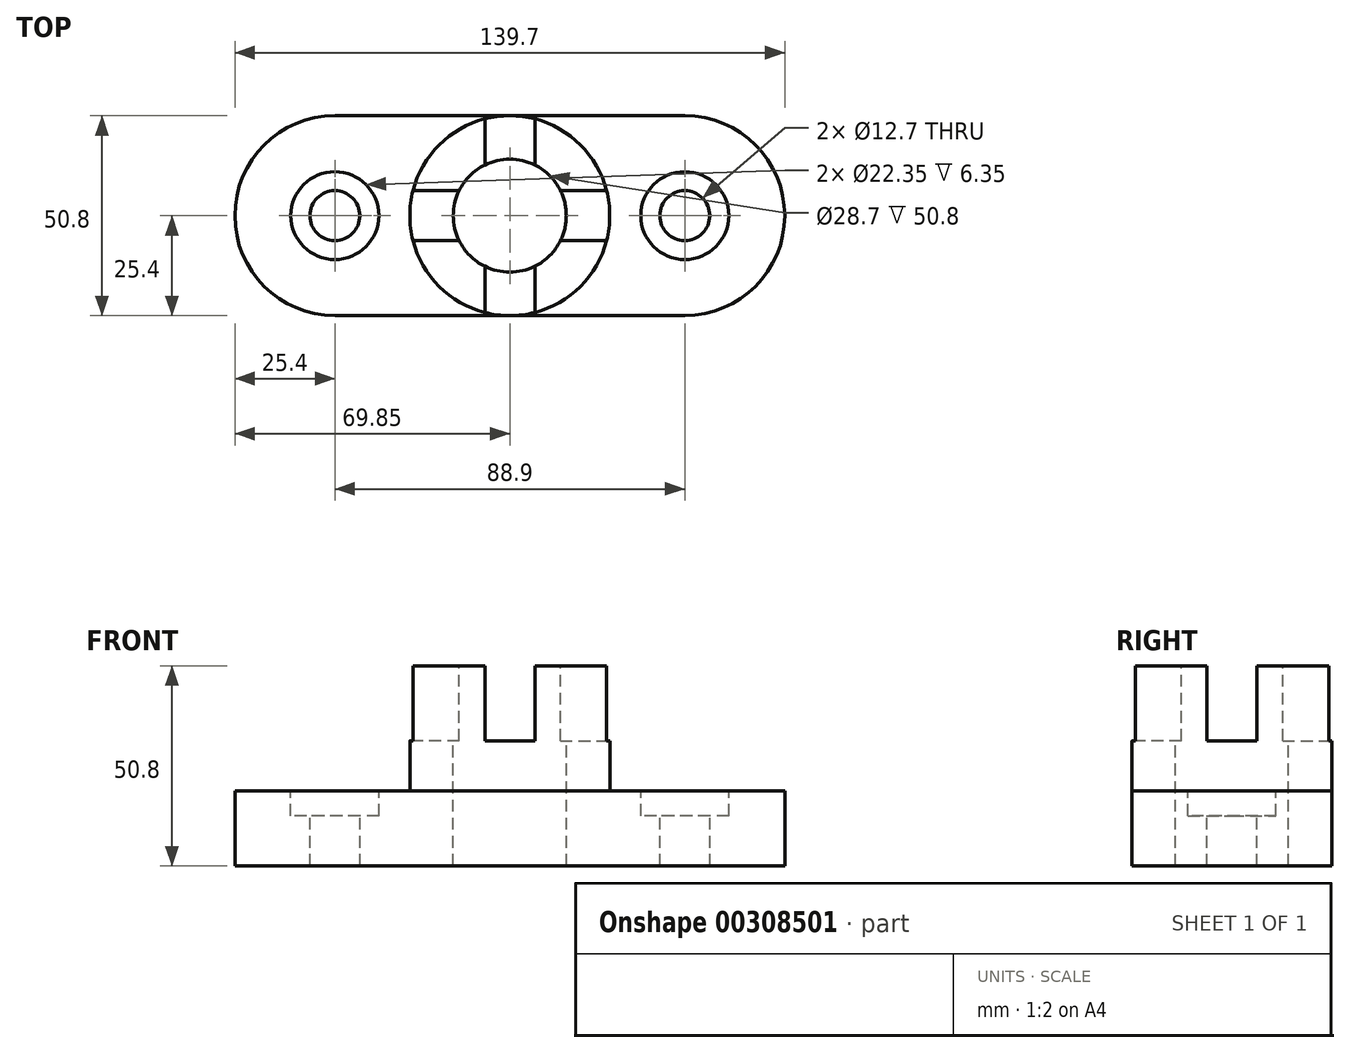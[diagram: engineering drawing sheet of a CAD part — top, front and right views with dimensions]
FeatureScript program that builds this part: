
annotation { "Feature Type Name" : "Feature", "Feature Type Description" : "" }
export const myFeature = defineFeature(function(context is Context, id is Id, definition is map)
    precondition{}
    {
        {
            var Q0;
            Q0=qCreatedBy(makeId("Top.planeOp"),FACE);
            var sketch = newSketch(context, id + "F0", { "sketchPlane" : qUnion([Q0])});
            skLineSegment(sketch, "E0.bottom", {"start": v(-44.45, -25.4) * mm, "end": v(44.45, -25.4) * mm, "construction": true});
            skLineSegment(sketch, "E0.top", {"start": v(-44.45, 25.4) * mm, "end": v(44.45, 25.4) * mm, "construction": true});
            skLineSegment(sketch, "E0.left", {"start": v(-44.45, -25.4) * mm, "end": v(-44.45, 25.4) * mm, "construction": true});
            skLineSegment(sketch, "E0.right", {"start": v(44.45, -25.4) * mm, "end": v(44.45, 25.4) * mm, "construction": true});
            skLineSegment(sketch, "E1.bottom", {"start": v(-69.85, -25.4) * mm, "end": v(69.85, -25.4) * mm, "construction": true});
            skLineSegment(sketch, "E1.top", {"start": v(-69.85, 25.4) * mm, "end": v(69.85, 25.4) * mm, "construction": true});
            skLineSegment(sketch, "E1.left", {"start": v(-69.85, -25.4) * mm, "end": v(-69.85, 25.4) * mm, "construction": true});
            skLineSegment(sketch, "E1.right", {"start": v(69.85, -25.4) * mm, "end": v(69.85, 25.4) * mm, "construction": true});
            skLineSegment(sketch, "E2", {"start": v(-69.85, 0) * mm, "end": v(69.85, 0) * mm, "construction": true});
            skLineSegment(sketch, "E3", {"start": v(-44.45, -25.4) * mm, "end": v(44.45, -25.4) * mm});
            skLineSegment(sketch, "E4", {"start": v(44.45, 25.4) * mm, "end": v(-44.45, 25.4) * mm});
            skArc(sketch, "E5", {"start": v(-44.45, 25.4) * mm, "mid": v(-69.85, 0) * mm, "end": v(-44.45, -25.4) * mm});
            skArc(sketch, "E6", {"start": v(44.45, -25.4) * mm, "mid": v(69.85, 0) * mm, "end": v(44.45, 25.4) * mm});
            skCircle(sketch, "E7", {"center": v(-44.45, 0) * mm, "radius": 11.18 * mm});
            skCircle(sketch, "E8", {"center": v(44.45, 0) * mm, "radius": 11.18 * mm});
            skCircle(sketch, "E9", {"center": v(44.45, 0) * mm, "radius": 6.35 * mm});
            skCircle(sketch, "E10", {"center": v(-44.45, 0) * mm, "radius": 6.35 * mm});
            skCircle(sketch, "E11", {"center": v(0, 0) * mm, "radius": 25.4 * mm});
            skSolve(sketch);
        }
        {
            var Q0;
            Q0=makeQuery(id+"F0.imprint","IMPRINT",FACE,{"disambiguationData":[TD([[makeQuery(id+"F0.imprint","IMPRINT",EDGE,{"derivedFrom":sQuery(id+"F0.wireOp",EDGE,"E3")}),1.0]])]});
            var Q1;
            Q1=makeQuery(id+"F0.imprint","IMPRINT",FACE,{"disambiguationData":[TD([[makeQuery(id+"F0.imprint","IMPRINT",EDGE,{"derivedFrom":sQuery(id+"F0.wireOp",EDGE,"E7")}),1.0]])]});
            var Q2;
            Q2=makeQuery(id+"F0.imprint","IMPRINT",FACE,{"disambiguationData":[TD([[makeQuery(id+"F0.imprint","IMPRINT",EDGE,{"derivedFrom":sQuery(id+"F0.wireOp",EDGE,"E8")}),1.0]])]});
            var Q3;
            {var subQ0=sQuery(id+"F0.wireOp",EDGE,"E11");var subQ1=makeQuery(id+"F0.imprint","INTERSECT",VERTEX,{"derivedFrom":[sQuery(id+"F0.wireOp",EDGE,"E3"),subQ0]});Q3=makeQuery(id+"F0.imprint","IMPRINT",FACE,{"disambiguationData":[TD([[makeQuery(id+"F0.imprint","IMPRINT",EDGE,{"disambiguationData":[TD([[subQ1,1.0]])],"derivedFrom":subQ0}),1.0]])]});}
            extrude(context, id + "F1", {"entities" : qUnion([Q0, Q1, Q2, Q3]), "oppositeDirection" : true, "depth" : 19.05 * mm});
        }
        {
            var Q0;
            Q0=makeQuery(id+"F0.imprint","IMPRINT",FACE,{"disambiguationData":[TD([[makeQuery(id+"F0.imprint","IMPRINT",EDGE,{"derivedFrom":sQuery(id+"F0.wireOp",EDGE,"E7")}),1.0]])]});
            var Q1;
            Q1=makeQuery(id+"F0.imprint","IMPRINT",FACE,{"disambiguationData":[TD([[makeQuery(id+"F0.imprint","IMPRINT",EDGE,{"derivedFrom":sQuery(id+"F0.wireOp",EDGE,"E8")}),1.0]])]});
            extrude(context, id + "F2", {"entities" : qUnion([Q0, Q1]), "operationType" : NewBodyOperationType.REMOVE, "oppositeDirection" : true, "depth" : 6.35 * mm});
        }
        {
            var Q0;
            {var subQ0=sQuery(id+"F0.wireOp",EDGE,"E11");var subQ1=makeQuery(id+"F0.imprint","INTERSECT",VERTEX,{"derivedFrom":[sQuery(id+"F0.wireOp",EDGE,"E3"),subQ0]});Q0=makeQuery(id+"F0.imprint","IMPRINT",FACE,{"disambiguationData":[TD([[makeQuery(id+"F0.imprint","IMPRINT",EDGE,{"disambiguationData":[TD([[subQ1,1.0]])],"derivedFrom":subQ0}),1.0]])]});}
            extrude(context, id + "F3", {"entities" : qUnion([Q0]), "operationType" : NewBodyOperationType.ADD, "depth" : 31.75 * mm});
        }
        {
            var Q0;
            Q0=makeQuery(id+"F3.opExtrude","CAP_FACE",FACE,{"disambiguationData":[OSD([sQuery(id+"F0.wireOp",EDGE,"E11")])],"isStart":false});
            var sketch = newSketch(context, id + "F4", { "sketchPlane" : qUnion([Q0])});
            skCircle(sketch, "E12", {"center": v(0, 0) * mm, "radius": 14.35 * mm});
            skLineSegment(sketch, "E13", {"start": v(0, 25.4) * mm, "end": v(0, -25.4) * mm, "construction": true});
            skLineSegment(sketch, "E14", {"start": v(25.4, 0) * mm, "end": v(-25.4, 0) * mm, "construction": true});
            skLineSegment(sketch, "E15", {"start": v(6.35, 12.87) * mm, "end": v(6.35, 24.6) * mm});
            skLineSegment(sketch, "E16", {"start": v(12.87, 6.35) * mm, "end": v(24.6, 6.35) * mm});
            skLineSegment(sketch, "E17.MirrorCS", {"start": v(-6.35, 12.87) * mm, "end": v(-6.35, 24.6) * mm});
            skLineSegment(sketch, "E18.MirrorCS", {"start": v(-6.35, -12.87) * mm, "end": v(-6.35, -24.6) * mm});
            skLineSegment(sketch, "E19.MirrorCS", {"start": v(6.35, -12.87) * mm, "end": v(6.35, -24.6) * mm});
            skLineSegment(sketch, "E20.MirrorCS", {"start": v(12.87, -6.35) * mm, "end": v(24.6, -6.35) * mm});
            skLineSegment(sketch, "E21.MirrorCS", {"start": v(-12.87, 6.35) * mm, "end": v(-24.6, 6.35) * mm});
            skLineSegment(sketch, "E22.MirrorCS", {"start": v(-12.87, -6.35) * mm, "end": v(-24.6, -6.35) * mm});
            skSolve(sketch);
        }
        {
            var Q0;
            {var subQ0=sQuery(id+"F4.wireOp",EDGE,"E18.MirrorCS");Q0=makeQuery(id+"F4.imprint","IMPRINT",FACE,{"disambiguationData":[TD([[makeQuery(id+"F4.imprint","IMPRINT",EDGE,{"derivedFrom":subQ0}),1.0]])]});}
            var Q1;
            {var subQ0=sQuery(id+"F4.wireOp",EDGE,"E21.MirrorCS");Q1=makeQuery(id+"F4.imprint","IMPRINT",FACE,{"disambiguationData":[TD([[makeQuery(id+"F4.imprint","IMPRINT",EDGE,{"derivedFrom":subQ0}),1.0]])]});}
            var Q2;
            {var subQ0=sQuery(id+"F4.wireOp",EDGE,"E15");Q2=makeQuery(id+"F4.imprint","IMPRINT",FACE,{"disambiguationData":[TD([[makeQuery(id+"F4.imprint","IMPRINT",EDGE,{"derivedFrom":subQ0}),1.0]])]});}
            var Q3;
            {var subQ0=sQuery(id+"F4.wireOp",EDGE,"E16");Q3=makeQuery(id+"F4.imprint","IMPRINT",FACE,{"disambiguationData":[TD([[makeQuery(id+"F4.imprint","IMPRINT",EDGE,{"derivedFrom":subQ0}),-1.0]])]});}
            extrude(context, id + "F5", {"entities" : qUnion([Q0, Q1, Q2, Q3]), "operationType" : NewBodyOperationType.REMOVE, "oppositeDirection" : true, "depth" : 19.05 * mm});
        }
        {
            var Q0;
            {var subQ0=sQuery(id+"F4.wireOp",EDGE,"E12");var subQ4=makeQuery(id+"F4.imprint","INTERSECT",VERTEX,{"derivedFrom":[subQ0,sQuery(id+"F4.wireOp",EDGE,"E15")]});Q0=makeQuery(id+"F4.imprint","IMPRINT",FACE,{"disambiguationData":[TD([[makeQuery(id+"F4.imprint","IMPRINT",EDGE,{"disambiguationData":[TD([[subQ4,1.0]])],"derivedFrom":subQ0}),1.0]])]});}
            var Q1;
            Q1=makeQuery(id+"F1.opExtrude","CAP_FACE",FACE,{"disambiguationData":[OSD([sQuery(id+"F0.wireOp",EDGE,"E3"),sQuery(id+"F0.wireOp",EDGE,"E4"),sQuery(id+"F0.wireOp",EDGE,"E5"),sQuery(id+"F0.wireOp",EDGE,"E6"),sQuery(id+"F0.wireOp",EDGE,"E9"),sQuery(id+"F0.wireOp",EDGE,"E10")])],"isStart":false});
            extrude(context, id + "F6", {"entities" : qUnion([Q0]), "operationType" : NewBodyOperationType.REMOVE, "endBound" : BoundingType.UP_TO_SURFACE, "oppositeDirection" : true, "endBoundEntityFace" : qUnion([Q1]), "depth" : 25.4 * mm});
        }
    });
